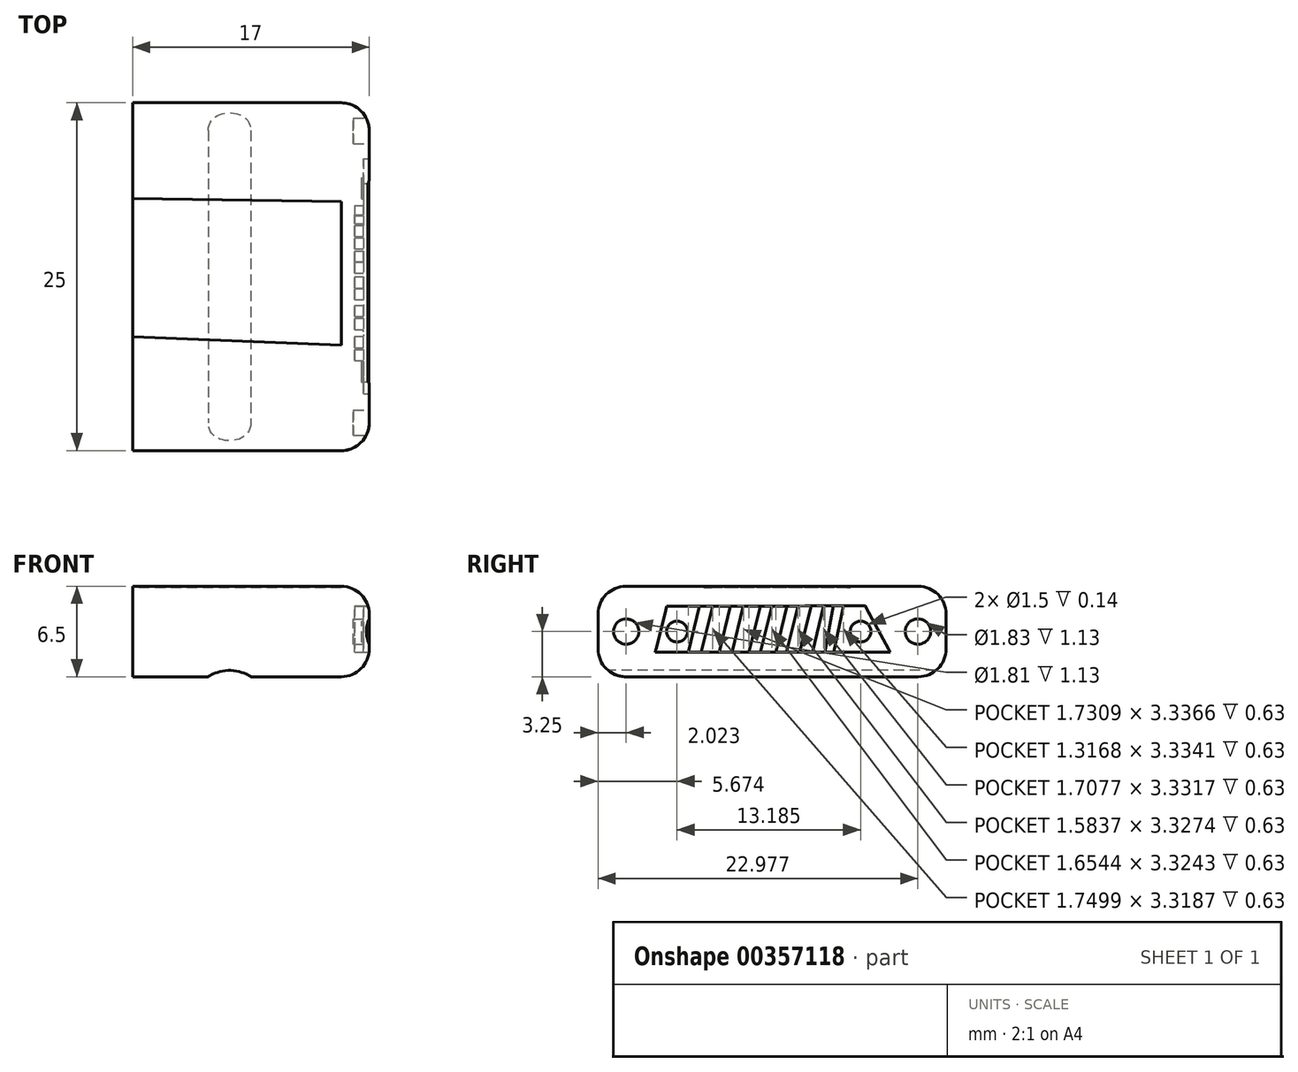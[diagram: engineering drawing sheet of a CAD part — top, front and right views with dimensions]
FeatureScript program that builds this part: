
annotation { "Feature Type Name" : "Feature", "Feature Type Description" : "" }
export const myFeature = defineFeature(function(context is Context, id is Id, definition is map)
    precondition{}
    {
        {
            var Q0;
            Q0=qCreatedBy(makeId("Top.planeOp"),FACE);
            var sketch = newSketch(context, id + "F0", { "sketchPlane" : qUnion([Q0])});
            skLineSegment(sketch, "E0.bottom", {"start": v(-8.5, 12.5) * mm, "end": v(8.5, 12.5) * mm});
            skLineSegment(sketch, "E0.top", {"start": v(-8.5, -12.5) * mm, "end": v(8.5, -12.5) * mm});
            skLineSegment(sketch, "E0.left", {"start": v(-8.5, 12.5) * mm, "end": v(-8.5, -12.5) * mm});
            skLineSegment(sketch, "E0.right", {"start": v(8.5, 12.5) * mm, "end": v(8.5, -12.5) * mm});
            skPoint(sketch, "E0.middle", {"position": v(0, 0) * mm});
            skSolve(sketch);
        }
        {
            var Q0;
            Q0 = qSketchRegion(id + "F0", true);
            extrude(context, id + "F1", {"entities" : qUnion([Q0]), "endBound" : BoundingType.SYMMETRIC, "depth" : 6.5 * mm});
        }
        {
            var Q0;
            Q0=makeQuery(id+"F1.opExtrude","SWEPT_FACE",FACE,{"disambiguationData":[OSD([sQuery(id+"F0.wireOp",EDGE,"E0.top")])]});
            var sketch = newSketch(context, id + "F2", { "sketchPlane" : qUnion([Q0])});
            skArc(sketch, "E1", {"start": v(0, -3.25) * mm, "mid": v(-1.53, -2.79) * mm, "end": v(-3.06, -3.25) * mm});
            skLineSegment(sketch, "E2", {"start": v(-3.06, -3.25) * mm, "end": v(0, -3.25) * mm});
            skSolve(sketch);
        }
        {
            var Q0;
            Q0 = qSketchRegion(id + "F2", true);
            extrude(context, id + "F3", {"entities" : qUnion([Q0]), "operationType" : NewBodyOperationType.REMOVE, "oppositeDirection" : true, "depth" : 29 * mm});
        }
        {
            var Q0;
            Q0=makeQuery(id+"F1.opExtrude","CAP_EDGE",EDGE,{"disambiguationData":[OSD([sQuery(id+"F0.wireOp",EDGE,"E0.top")])],"isStart":false});
            fillet(context, id + "F4", {"entities" : qUnion([Q0]), "radius" : 2 * mm, "tangentPropagation" : true, "allowEdgeOverflow" : false});
        }
        {
            var Q0;
            Q0=makeQuery(id+"F1.opExtrude","CAP_EDGE",EDGE,{"disambiguationData":[OSD([sQuery(id+"F0.wireOp",EDGE,"E0.bottom")])],"isStart":false});
            fillet(context, id + "F5", {"entities" : qUnion([Q0]), "radius" : 2 * mm, "tangentPropagation" : true, "allowEdgeOverflow" : false});
        }
        {
            var Q0;
            Q0=makeQuery(id+"F1.opExtrude","CAP_EDGE",EDGE,{"disambiguationData":[OSD([sQuery(id+"F0.wireOp",EDGE,"E0.right")])],"isStart":false});
            fillet(context, id + "F6", {"entities" : qUnion([Q0]), "radius" : 2 * mm, "tangentPropagation" : true, "allowEdgeOverflow" : false});
        }
        {
            var Q0;
            Q0=makeQuery(id+"F1.opExtrude","CAP_EDGE",EDGE,{"disambiguationData":[OSD([sQuery(id+"F0.wireOp",EDGE,"E0.right")])],"isStart":true});
            fillet(context, id + "F7", {"entities" : qUnion([Q0]), "radius" : 2 * mm, "tangentPropagation" : true, "allowEdgeOverflow" : false});
        }
        {
            var Q0;
            Q0=makeQuery(id+"F1.opExtrude","SWEPT_FACE",FACE,{"disambiguationData":[OSD([sQuery(id+"F0.wireOp",EDGE,"E0.right")])]});
            var sketch = newSketch(context, id + "F8", { "sketchPlane" : qUnion([Q0])});
            skCircle(sketch, "E3", {"center": v(-10.48, 0) * mm, "radius": 0.9 * mm});
            skCircle(sketch, "E4", {"center": v(10.48, 0) * mm, "radius": 0.91 * mm});
            skSolve(sketch);
        }
        {
            var Q0;
            Q0 = qSketchRegion(id + "F8", true);
            extrude(context, id + "F9", {"entities" : qUnion([Q0]), "operationType" : NewBodyOperationType.REMOVE, "oppositeDirection" : true, "depth" : 1.13 * mm});
        }
        {
            var Q0;
            Q0=makeQuery(id+"F1.opExtrude","SWEPT_FACE",FACE,{"disambiguationData":[OSD([sQuery(id+"F0.wireOp",EDGE,"E0.right")])]});
            var sketch = newSketch(context, id + "F10", { "sketchPlane" : qUnion([Q0])});
            skLineSegment(sketch, "E5", {"start": v(-7.56, 1.82) * mm, "end": v(-8.4, -1.5) * mm});
            skLineSegment(sketch, "E6", {"start": v(-8.4, -1.5) * mm, "end": v(8.5, -1.5) * mm});
            skLineSegment(sketch, "E7", {"start": v(8.5, -1.5) * mm, "end": v(6.7, 1.84) * mm});
            skLineSegment(sketch, "E8", {"start": v(6.7, 1.84) * mm, "end": v(-7.56, 1.82) * mm});
            skSolve(sketch);
        }
        {
            var Q0;
            Q0 = qSketchRegion(id + "F10", true);
            extrude(context, id + "F11", {"entities" : qUnion([Q0]), "operationType" : NewBodyOperationType.REMOVE, "oppositeDirection" : true, "depth" : 0.4 * mm});
        }
        {
            var Q0;
            Q0=makeQuery(id+"F11.boolean.opBoolean","COPY",FACE,{"derivedFrom":makeQuery(id+"F11.opExtrude","CAP_FACE",FACE,{"disambiguationData":[OSD([sQuery(id+"F10.wireOp",EDGE,"E5"),sQuery(id+"F10.wireOp",EDGE,"E6"),sQuery(id+"F10.wireOp",EDGE,"E7"),sQuery(id+"F10.wireOp",EDGE,"E8")])],"isStart":false})});
            var sketch = newSketch(context, id + "F12", { "sketchPlane" : qUnion([Q0])});
            skCircle(sketch, "E9", {"center": v(-6.83, 0) * mm, "radius": 0.75 * mm});
            skCircle(sketch, "E10", {"center": v(6.36, 0) * mm, "radius": 0.75 * mm});
            skSolve(sketch);
        }
        {
            var Q0;
            Q0 = qSketchRegion(id + "F12", true);
            extrude(context, id + "F13", {"entities" : qUnion([Q0]), "operationType" : NewBodyOperationType.REMOVE, "oppositeDirection" : true, "depth" : 0.14 * mm});
        }
        {
            var Q0;
            Q0=makeQuery(id+"F11.boolean.opBoolean","COPY",FACE,{"derivedFrom":makeQuery(id+"F11.opExtrude","CAP_FACE",FACE,{"disambiguationData":[OSD([sQuery(id+"F10.wireOp",EDGE,"E5"),sQuery(id+"F10.wireOp",EDGE,"E6"),sQuery(id+"F10.wireOp",EDGE,"E7"),sQuery(id+"F10.wireOp",EDGE,"E8")])],"isStart":false})});
            var sketch = newSketch(context, id + "F14", { "sketchPlane" : qUnion([Q0])});
            skLineSegment(sketch, "E11", {"start": v(-5.23, 1.82) * mm, "end": v(-6.03, -1.5) * mm});
            skLineSegment(sketch, "E12", {"start": v(-6.03, -1.5) * mm, "end": v(-5.1, -1.5) * mm});
            skLineSegment(sketch, "E13", {"start": v(-5.1, -1.5) * mm, "end": v(-4.28, 1.83) * mm});
            skLineSegment(sketch, "E14", {"start": v(-4.28, 1.83) * mm, "end": v(-5.23, 1.82) * mm});
            skLineSegment(sketch, "E15", {"start": v(-2.99, 1.83) * mm, "end": v(-3.8, -1.5) * mm});
            skLineSegment(sketch, "E16", {"start": v(-3.8, -1.5) * mm, "end": v(-2.87, -1.5) * mm});
            skLineSegment(sketch, "E17", {"start": v(-2.87, -1.5) * mm, "end": v(-2.06, 1.84) * mm});
            skLineSegment(sketch, "E18", {"start": v(-2.06, 1.84) * mm, "end": v(-2.99, 1.83) * mm});
            skLineSegment(sketch, "E19", {"start": v(-0.85, 1.83) * mm, "end": v(-1.65, -1.5) * mm});
            skLineSegment(sketch, "E20", {"start": v(-1.65, -1.5) * mm, "end": v(-0.83, -1.5) * mm});
            skLineSegment(sketch, "E21", {"start": v(-0.83, -1.5) * mm, "end": v(0, 1.82) * mm});
            skLineSegment(sketch, "E22", {"start": v(0, 1.82) * mm, "end": v(-0.85, 1.83) * mm});
            skLineSegment(sketch, "E23", {"start": v(1.07, 1.83) * mm, "end": v(0.27, -1.5) * mm});
            skLineSegment(sketch, "E24", {"start": v(0.27, -1.5) * mm, "end": v(1.05, -1.5) * mm});
            skLineSegment(sketch, "E25", {"start": v(1.05, -1.5) * mm, "end": v(1.85, 1.83) * mm});
            skLineSegment(sketch, "E26", {"start": v(1.85, 1.83) * mm, "end": v(1.07, 1.83) * mm});
            skLineSegment(sketch, "E27", {"start": v(2.8, 1.84) * mm, "end": v(2, -1.5) * mm});
            skLineSegment(sketch, "E28", {"start": v(2, -1.5) * mm, "end": v(2.9, -1.5) * mm});
            skLineSegment(sketch, "E29", {"start": v(2.9, -1.5) * mm, "end": v(3.7, 1.84) * mm});
            skLineSegment(sketch, "E30", {"start": v(3.7, 1.84) * mm, "end": v(2.8, 1.84) * mm});
            skLineSegment(sketch, "E31", {"start": v(4.44, -1.5) * mm, "end": v(3.81, -1.5) * mm});
            skLineSegment(sketch, "E32", {"start": v(4.4, 1.84) * mm, "end": v(3.81, -1.5) * mm});
            skLineSegment(sketch, "E33", {"start": v(5.13, 1.84) * mm, "end": v(4.44, -1.5) * mm});
            skLineSegment(sketch, "E34", {"start": v(3.81, -1.5) * mm, "end": v(4.44, -1.5) * mm});
            skLineSegment(sketch, "E35", {"start": v(4.4, 1.84) * mm, "end": v(5.13, 1.84) * mm});
            skSolve(sketch);
        }
        {
            var Q0;
            Q0 = qSketchRegion(id + "F14", true);
            extrude(context, id + "F15", {"entities" : qUnion([Q0]), "operationType" : NewBodyOperationType.REMOVE, "oppositeDirection" : true, "depth" : 0.63 * mm});
        }
        {
            var Q0;
            Q0=makeQuery(id+"F1.opExtrude","CAP_FACE",FACE,{"disambiguationData":[OSD([sQuery(id+"F0.wireOp",EDGE,"E0.bottom"),sQuery(id+"F0.wireOp",EDGE,"E0.top"),sQuery(id+"F0.wireOp",EDGE,"E0.left"),sQuery(id+"F0.wireOp",EDGE,"E0.right")])],"isStart":false});
            var sketch = newSketch(context, id + "F16", { "sketchPlane" : qUnion([Q0])});
            skLineSegment(sketch, "E36", {"start": v(6.5, -4.9) * mm, "end": v(-8.5, -4.32) * mm});
            skLineSegment(sketch, "E37", {"start": v(6.5, 5.4) * mm, "end": v(-8.5, 5.62) * mm});
            skLineSegment(sketch, "E38", {"start": v(6.5, -4.9) * mm, "end": v(6.5, 5.4) * mm});
            skLineSegment(sketch, "E39", {"start": v(-8.5, -4.32) * mm, "end": v(-8.5, 5.62) * mm});
            skSolve(sketch);
        }
        {
            var Q0;
            Q0 = qSketchRegion(id + "F16", true);
            extrude(context, id + "F17", {"entities" : qUnion([Q0]), "operationType" : NewBodyOperationType.REMOVE, "oppositeDirection" : true, "depth" : 0.1 * mm});
        }
    });
